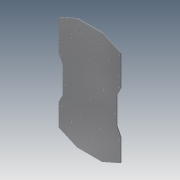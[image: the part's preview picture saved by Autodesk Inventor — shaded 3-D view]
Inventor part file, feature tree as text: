
AUTODESK INVENTOR PART (.ipt)
format: ipt  version: 2013 (Build 170138000, 138)  size: 150,016 bytes
history: native  units: mm
features: extrude x1, sketch x1
ambient origin geometry x8: Origin, YZ Plane, XZ Plane, XY Plane, X Axis, Y Axis, Z Axis, Center Point
bodies: Solid1 (feature_tree)
feature tree (2):
  extrude  "Extrusion1"  Depth=4.0mm
  sketch  "Sketch1"  dims[d0=4.0mm d1=4.0mm d2=4.0mm d3=4.0mm d4=4.0mm d5=4.0mm d6=4.0mm d7=4.0mm d8=4.0mm d9=4.0mm d10=4.0mm d11=4.0mm d12=4.0mm d13=4.0mm d14=4.0mm d15=4.0mm d16=4.0mm d17=4.0mm d18=4.0mm d19=4.0mm d20=4.0mm d21=4.0mm d22=4.0mm d23=4.0mm d24=4.0mm d25=2.0mm d26=0.0mm]
